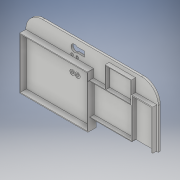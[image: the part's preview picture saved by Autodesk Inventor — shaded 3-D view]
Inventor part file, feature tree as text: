
AUTODESK INVENTOR PART (.ipt)
format: ipt  version: 2018 (Build 220112000, 112)  size: 308,224 bytes
history: native  units: in
note: dims shown in document units (in); Inventor stores cm internally (conversion verified against a paired STEP export)
features: sketch x21, extrude x18, fillet x4, plane x3, shell x2
ambient origin geometry x8: Origin, YZ Plane, XZ Plane, XY Plane, X Axis, Y Axis, Z Axis, Center Point
bodies: Solid1 (feature_tree)
feature tree (48):
  extrude  "Extrusion1"  Depth=3.4375in
  sketch  "Sketch2"  dims[d5=0.8125in d59=0.2in d60=0.0in d61=0.03in]
  fillet  "Fillet1"  Radius=0.1in
  fillet  "Fillet2"  Radius=0.8125in
  sketch  "Sketch8"  dims[d62=1.29in d63=1.038in d64=0.2in d65=0.0in]
  sketch  "Sketch11"  dims[d66=0.03in d77=0.35in]
  extrude  "Extrusion6"  Depth=0.2in TaperAngle=0.0deg
  shell  "Shell5"  Thickness=0.03in
  extrude  "Extrusion7"  Depth=1.038in
  shell  "Shell6"  Thickness=0.2in
  sketch  "Sketch20"  dims[d137=0.65in d138=2.375in]
  extrude  "Extrusion13"  Depth=0.03in
  sketch  "Sketch25"  dims[d149=0.75in d150=0.4375in]
  sketch  "Sketch27"  dims[d151=1.563in d154=0.75in]
  plane  "Work Plane1"
  sketch  "Sketch28"  dims[d155=0.125in d156=0.75in d157=0.25in d160=0.1in d161=0.0in]
  plane  "Work Plane2"
  extrude  "Extrusion16"  Depth=0.3in TaperAngle=0.0deg
  plane  "Work Plane3"
  sketch  "Sketch30"  dims[d164=0.75in d179=0.07in d180=0.0in]
  extrude  "Extrusion20"  Depth=0.125in
  extrude  "Extrusion21"  Depth=2.375in
  extrude  "Extrusion22"  Depth=0.25in
  extrude  "Extrusion23"  Depth=0.4375in
  extrude  "Extrusion24"  Depth=1.563in
  extrude  "Extrusion25"  Depth=0.1in
  fillet  "Fillet4"  Radius=0.25in
  fillet  "Fillet5"  Radius=0.1in
  extrude  "Extrusion26"  Depth=0.25in
  extrude  "Extrusion27"  Depth=0.07in TaperAngle=0.0deg
  extrude  "Extrusion28"  Depth=0.4in
  extrude  "Extrusion29"  Depth=1.0913in
  extrude  "Extrusion30"  Depth=0.3in TaperAngle=0.0deg
  extrude  "Extrusion31"  Depth=0.3in TaperAngle=0.0deg
  extrude  "Extrusion32"  Depth=0.8125in
  sketch  "Sketch1"  dims[d0=6.45in d1=3.4375in d2=0.1in d3=0.0in d4=0.8125in]
  sketch  "Sketch15"  dims[d114=3.2975in d116=0.3in d117=0.0in]
  sketch  "Sketch16"  dims[d126=0.125in d136=2.0688in]
  sketch  "Sketch24"  dims[d139=2.2558in d141=0.25in]
  sketch  "Sketch29"  dims[d162=0.25in d163=0.75in]
  sketch  "Sketch33"  dims[d181=1.65in d182=0.4in]
  sketch  "Sketch34"  dims[d183=1.1in d184=1.0913in]
  sketch  "Sketch35"  dims[d187=0.1in d188=0.0in d189=0.3in d190=0.0in]
  sketch  "Sketch36"  dims[d191=0.3in d192=0.0in d193=0.3in d194=0.0in]
  sketch  "Sketch37"  dims[d195=0.3in d196=0.0in d197=0.8125in]
  sketch  "Sketch38"  dims[d198=0.8125in]
  sketch  "Sketch39"  dims[d199=1.06in]
  sketch  "Sketch40"  dims[d200=1.95in d201=0.2in d202=0.0in d203=0.9375in d204=0.05in d205=0.05in d207=2.0in d208=0.2in d209=0.0in d210=0.825in d211=3.258in d212=2.4543in d213=0.03in d214=0.12in d215=0.3in d216=0.0in d217=0.1in d218=0.0in d219=0.5in d220=0.0in d221=0.0in d222=0.1in d223=0.3in d224=0.0in d225=0.0in d226=0.04in d227=0.5in d228=0.0in d229=0.65in d230=0.0in d231=0.0in]
